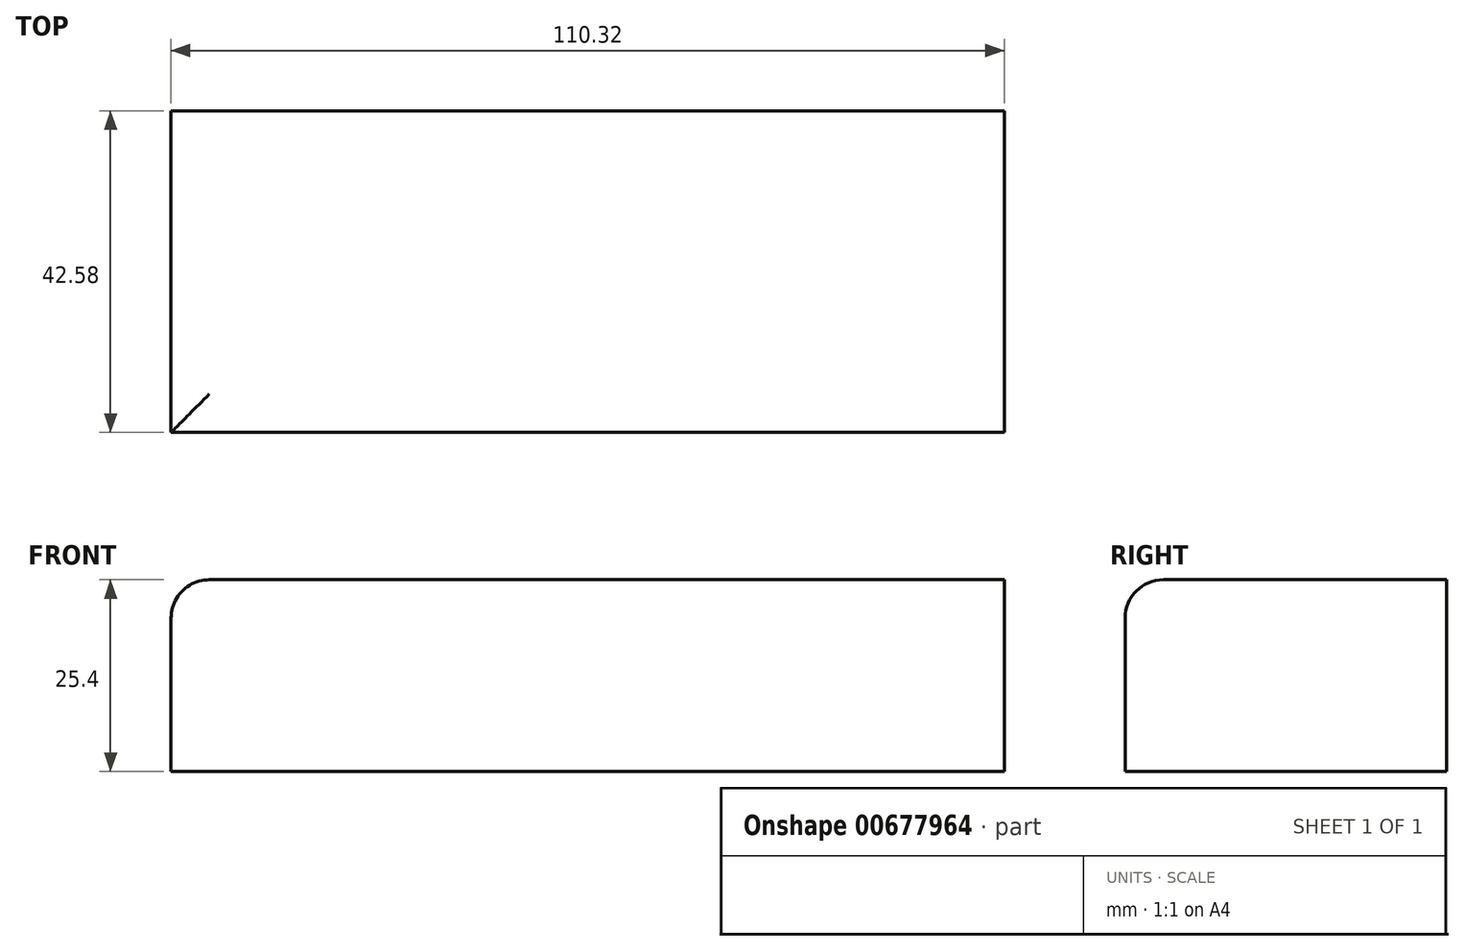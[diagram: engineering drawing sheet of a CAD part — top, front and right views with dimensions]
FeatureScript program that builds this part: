
annotation { "Feature Type Name" : "Feature", "Feature Type Description" : "" }
export const myFeature = defineFeature(function(context is Context, id is Id, definition is map)
    precondition{}
    {
        {
            var Q0;
            Q0=qCreatedBy(makeId("Top.planeOp"),FACE);
            var sketch = newSketch(context, id + "F0", { "sketchPlane" : qUnion([Q0])});
            skLineSegment(sketch, "E0.bottom", {"start": v(-97.2, -7.54) * mm, "end": v(13.13, -7.54) * mm});
            skLineSegment(sketch, "E0.top", {"start": v(-97.2, -50.12) * mm, "end": v(13.13, -50.12) * mm});
            skLineSegment(sketch, "E0.left", {"start": v(-97.2, -7.54) * mm, "end": v(-97.2, -50.12) * mm});
            skLineSegment(sketch, "E0.right", {"start": v(13.13, -7.54) * mm, "end": v(13.13, -50.12) * mm});
            skSolve(sketch);
        }
        {
            var Q0;
            Q0=makeQuery(id+"F0.imprint","IMPRINT",FACE,{"disambiguationData":[TD([[makeQuery(id+"F0.imprint","IMPRINT",EDGE,{"derivedFrom":sQuery(id+"F0.wireOp",EDGE,"E0.bottom")}),-1.0]])]});
            extrude(context, id + "F1", {"entities" : qUnion([Q0]), "depth" : 25.4 * mm, "offsetDistance" : 25.4 * mm});
        }
        {
            var Q0;
            Q0=makeQuery(id+"F1.opExtrude","CAP_EDGE",EDGE,{"disambiguationData":[OSD([sQuery(id+"F0.wireOp",EDGE,"E0.top")])],"isStart":false});
            var Q1;
            Q1=makeQuery(id+"F1.opExtrude","CAP_EDGE",EDGE,{"disambiguationData":[OSD([sQuery(id+"F0.wireOp",EDGE,"E0.left")])],"isStart":false});
            fillet(context, id + "F2", {"entities" : qUnion([Q0, Q1]), "radius" : 5.08 * mm, "tangentPropagation" : true, "allowEdgeOverflow" : false});
        }
    });
